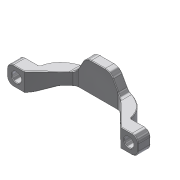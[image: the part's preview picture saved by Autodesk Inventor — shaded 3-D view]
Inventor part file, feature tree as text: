
AUTODESK INVENTOR PART (.ipt)
format: ipt  version: 2015 (Build 190159000, 159)  size: 524,288 bytes
history: native  units: mm
features: projected_geometry x13, fillet x12, sketch x7, extrude x5, hole x2, plane x2
ambient origin geometry x8: Origin, YZ Plane, XZ Plane, XY Plane, X Axis, Y Axis, Z Axis, Center Point
bodies: Volumenkörper1 (feature_tree)
feature tree (41):
  extrude  "Extrusion1"  Depth=8.2mm
  hole  "Bohrung1"  [1 undecoded]
  extrude  "Extrusion3"  Depth=3.0mm
  extrude  "Extrusion4"  Depth=4.0mm
  plane  "Arbeitsebene1"
  extrude  "Extrusion5"  Depth=5.5mm
  plane  "Arbeitsebene2"
  hole  "Bohrung2"  [1 undecoded]
  extrude  "Extrusion6"  Depth=6.5mm
  fillet  "Rundung15"  Radius=3.0mm
  fillet  "Rundung16"  Radius=8.0mm
  fillet  "Rundung17"  Radius=16.0mm
  fillet  "Rundung18"  Radius=3.0mm
  fillet  "Rundung19"  Radius=3.0mm
  fillet  "Rundung20"  Radius=5.5mm
  fillet  "Rundung21"  Radius=6.5mm
  fillet  "Rundung22"  Radius=7.0mm
  fillet  "Rundung24"  Radius=20.0mm
  fillet  "Rundung26"  Radius=2.0mm
  fillet  "Rundung28"  Radius=3.0mm
  fillet  "Rundung29"  Radius=3.0mm
  sketch  "Skizze1"  dims[d2=42.0mm d4=8.2mm]
  sketch  "Skizze2"  dims[d5=6.0mm d6=0.0mm d7=36.0mm]
  projected_geometry  "Projizierte Kontur1"
  projected_geometry  "Projizierte Kontur2"
  sketch  "Skizze4"  dims[d8=3.0mm d9=6.0mm d10=4.0mm d11=2.0mm d12=90.0deg d13=8.0mm d14=20.594885mm d15=3.0mm]
  projected_geometry  "Projizierte Kontur4"
  sketch  "Skizze5"  dims[d21=7.0mm d24=4.0mm]
  projected_geometry  "Projizierte Kontur5"
  projected_geometry  "Projizierte Kontur6"
  sketch  "Skizze6"  dims[d25=4.0mm d26=5.5mm]
  sketch  "Skizze7"  dims[d27=0.0mm d28=3.0mm d29=0.0mm]
  projected_geometry  "Projizierte Kontur7"
  projected_geometry  "Projizierte Kontur8"
  projected_geometry  "Projizierte Kontur9"
  sketch  "Skizze8"  dims[d30=6.5mm d31=6.5mm d32=3.0mm d33=0.0mm d36=8.0mm d37=16.0mm d38=3.0mm d47=3.0mm d48=0.0mm d53=5.5mm d54=6.5mm d55=7.0mm d56=1.5mm d57=6.0mm d58=4.0mm d59=2.0mm d60=90.0deg d61=8.0mm d62=20.594885mm d64=20.0mm d68=2.0mm d75=3.0mm d76=3.0mm d77=3.0mm d78=0.0mm d79=2.0mm d80=0.5mm d81=8.0mm d82=3.0mm d83=0.2mm d84=2.0mm d85=2.0mm d86=2.0mm d88=0.2mm d90=8.0mm d92=5.0mm d93=0.2mm]
  projected_geometry  "Projizierte Kontur10"
  projected_geometry  "Projizierte Kontur11"
  projected_geometry  "Projizierte Kontur12"
  projected_geometry  "Projizierte Kontur13"
  projected_geometry  "Projizierte Kontur14"
note: 2 required parameter values undecoded (feature->parameter linkage not recoverable at this tier; creation-order binding heuristic only, values carry confidence <= 0.55)
